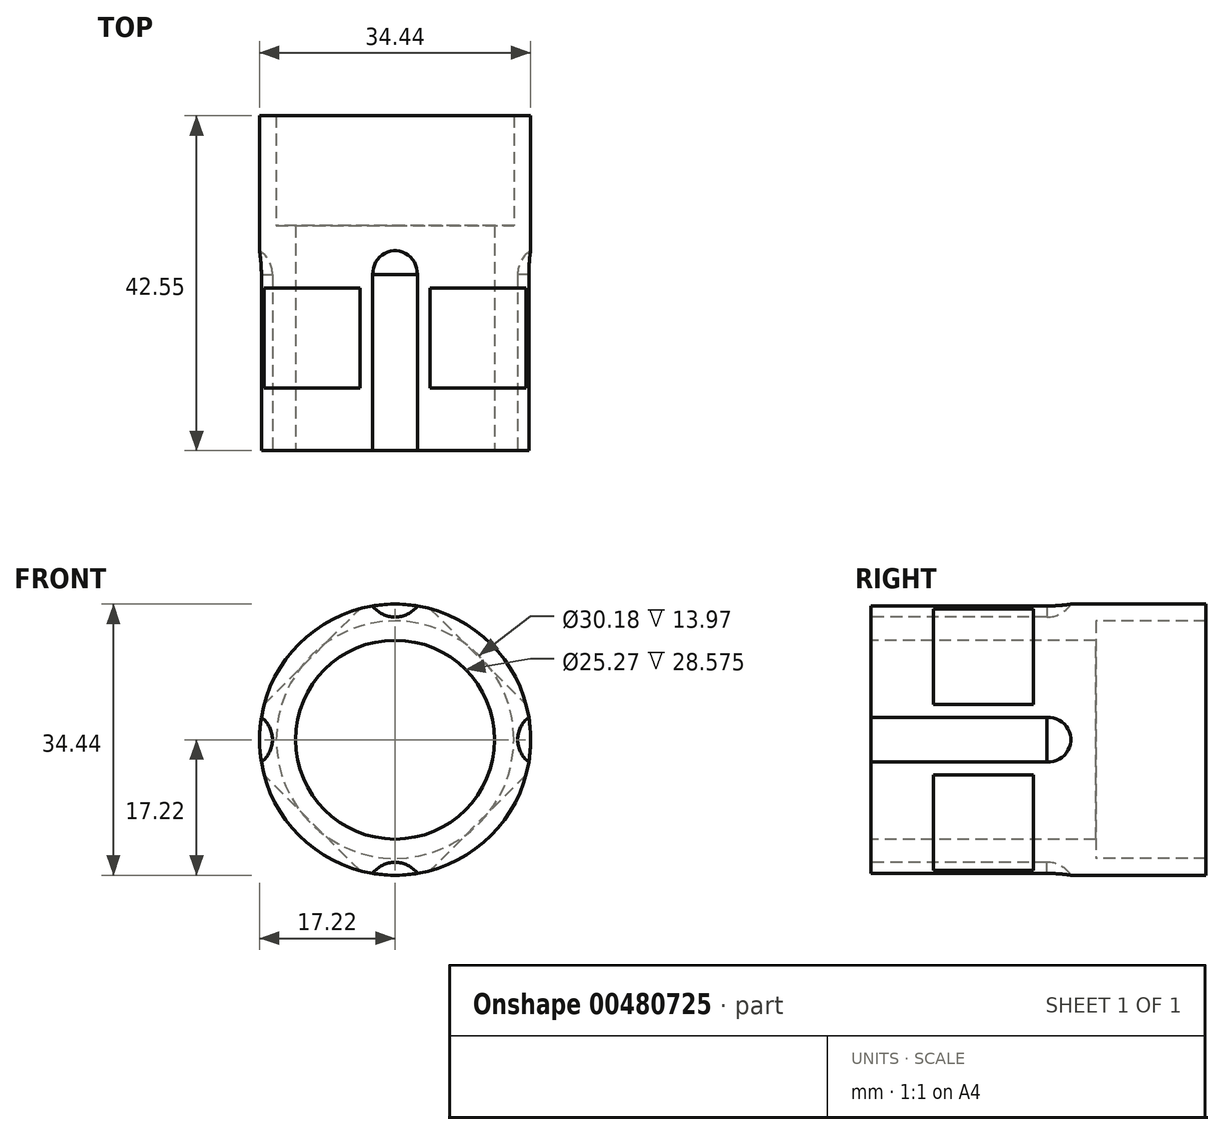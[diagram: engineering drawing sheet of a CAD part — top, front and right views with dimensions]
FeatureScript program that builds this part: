
annotation { "Feature Type Name" : "Feature", "Feature Type Description" : "" }
export const myFeature = defineFeature(function(context is Context, id is Id, definition is map)
    precondition{}
    {
        {
            var Q0;
            Q0=qCreatedBy(makeId("Front.planeOp"),FACE);
            var sketch = newSketch(context, id + "F0", { "sketchPlane" : qUnion([Q0])});
            skCircle(sketch, "E0", {"center": v(0, 0) * mm, "radius": 17.22 * mm});
            skCircle(sketch, "E1.cCircle", {"center": v(0, 0) * mm, "radius": 14.92 * mm, "construction": true});
            skLineSegment(sketch, "E1.0", {"start": v(-4.47, -16.63) * mm, "end": v(-16.63, -4.47) * mm});
            skLineSegment(sketch, "E1.1", {"start": v(-16.63, 4.47) * mm, "end": v(-4.47, 16.63) * mm});
            skLineSegment(sketch, "E1.2", {"start": v(4.47, 16.63) * mm, "end": v(16.63, 4.47) * mm});
            skLineSegment(sketch, "E1.3", {"start": v(16.63, -4.47) * mm, "end": v(4.47, -16.63) * mm});
            skPoint(sketch, "E1.0.midPoint", {"position": v(-10.55, -10.55) * mm});
            skPoint(sketch, "E2.orphan", {"position": v(0, 21.1) * mm});
            skPoint(sketch, "E3.orphan", {"position": v(21.1, 0) * mm});
            skPoint(sketch, "E4.orphan", {"position": v(0, -21.1) * mm});
            skPoint(sketch, "E5.orphan", {"position": v(-21.1, 0) * mm});
            skSolve(sketch);
        }
        {
            var Q0;
            {var subQ0=sQuery(id+"F0.wireOp",EDGE,"E1.0");Q0=makeQuery(id+"F0.imprint","IMPRINT",FACE,{"disambiguationData":[TD([[makeQuery(id+"F0.imprint","IMPRINT",EDGE,{"derivedFrom":subQ0}),-1.0]])]});}
            extrude(context, id + "F1", {"entities" : qUnion([Q0]), "depth" : 12.7 * mm});
        }
        {
            var Q0;
            Q0 = qSketchRegion(id + "F0", true);
            extrude(context, id + "F2", {"entities" : qUnion([Q0]), "operationType" : NewBodyOperationType.ADD, "oppositeDirection" : true, "depth" : 7.94 * mm});
        }
        {
            var Q0;
            Q0=makeQuery(id+"F2.opExtrude","CAP_FACE",FACE,{"disambiguationData":[OSD([sQuery(id+"F0.wireOp",EDGE,"E0")])],"isStart":false});
            var sketch = newSketch(context, id + "F3", { "sketchPlane" : qUnion([Q0])});
            skCircle(sketch, "E6", {"center": v(0, 0) * mm, "radius": 15.09 * mm});
            skSolve(sketch);
        }
        {
            var Q0;
            Q0=makeQuery(id+"F3.imprint","IMPRINT",FACE,{"disambiguationData":[TD([[makeQuery(id+"F3.imprint","IMPRINT",EDGE,{"derivedFrom":sQuery(id+"F3.wireOp",EDGE,"E6")}),-1.0]])]});
            extrude(context, id + "F4", {"entities" : qUnion([Q0]), "operationType" : NewBodyOperationType.ADD, "depth" : 13.97 * mm});
        }
        {
            var Q0;
            Q0=makeQuery(id+"F1.opExtrude","CAP_FACE",FACE,{"disambiguationData":[OSD([sQuery(id+"F0.wireOp",EDGE,"E0"),sQuery(id+"F0.wireOp",EDGE,"E1.0"),sQuery(id+"F0.wireOp",EDGE,"E1.1"),sQuery(id+"F0.wireOp",EDGE,"E1.2"),sQuery(id+"F0.wireOp",EDGE,"E1.3")])],"isStart":false});
            var sketch = newSketch(context, id + "F5", { "sketchPlane" : qUnion([Q0])});
            skCircle(sketch, "E7", {"center": v(0, 0) * mm, "radius": 17.22 * mm});
            skSolve(sketch);
        }
        {
            var Q0;
            Q0 = qSketchRegion(id + "F5", true);
            extrude(context, id + "F6", {"entities" : qUnion([Q0]), "operationType" : NewBodyOperationType.ADD, "depth" : 7.94 * mm});
        }
        {
            var Q0;
            Q0=makeQuery(id+"F6.opExtrude","CAP_FACE",FACE,{"disambiguationData":[OSD([sQuery(id+"F5.wireOp",EDGE,"E7")])],"isStart":false});
            var sketch = newSketch(context, id + "F7", { "sketchPlane" : qUnion([Q0])});
            skCircle(sketch, "E8", {"center": v(0, 0) * mm, "radius": 12.64 * mm});
            skSolve(sketch);
        }
        {
            var Q0;
            Q0 = qSketchRegion(id + "F7", true);
            extrude(context, id + "F8", {"entities" : qUnion([Q0]), "operationType" : NewBodyOperationType.REMOVE, "endBound" : BoundingType.THROUGH_ALL, "oppositeDirection" : true, "depth" : 25.4 * mm});
        }
        {
            var Q0;
            Q0=makeQuery(id+"F6.opExtrude","CAP_FACE",FACE,{"disambiguationData":[OSD([sQuery(id+"F5.wireOp",EDGE,"E7")])],"isStart":false});
            var sketch = newSketch(context, id + "F9", { "sketchPlane" : qUnion([Q0])});
            skCircle(sketch, "E9", {"center": v(-19.14, 0) * mm, "radius": 3.57 * mm});
            skCircle(sketch, "E10", {"center": v(0, 19.14) * mm, "radius": 3.57 * mm});
            skCircle(sketch, "E11", {"center": v(19.14, 0) * mm, "radius": 3.57 * mm});
            skCircle(sketch, "E12", {"center": v(0, -19.14) * mm, "radius": 3.57 * mm});
            skSolve(sketch);
        }
        {
            var Q0;
            Q0 = qSketchRegion(id + "F9", true);
            extrude(context, id + "F10", {"entities" : qUnion([Q0]), "operationType" : NewBodyOperationType.REMOVE, "oppositeDirection" : true, "depth" : 25.4 * mm});
        }
        {
            var Q0;
            Q0=makeQuery(id+"F10.boolean.opBoolean","COPY",EDGE,{"derivedFrom":makeQuery(id+"F10.opExtrude","CAP_EDGE",EDGE,{"disambiguationData":[OSD([sQuery(id+"F9.wireOp",EDGE,"E10")])],"isStart":false})});
            fillet(context, id + "F11", {"entities" : qUnion([Q0]), "radius" : 3.57 * mm, "tangentPropagation" : true, "allowEdgeOverflow" : false});
        }
        {
            var Q0;
            Q0=makeQuery(id+"F10.boolean.opBoolean","COPY",EDGE,{"derivedFrom":makeQuery(id+"F10.opExtrude","CAP_EDGE",EDGE,{"disambiguationData":[OSD([sQuery(id+"F9.wireOp",EDGE,"E9")])],"isStart":false})});
            fillet(context, id + "F12", {"entities" : qUnion([Q0]), "radius" : 3.57 * mm, "tangentPropagation" : true, "allowEdgeOverflow" : false});
        }
        {
            var Q0;
            Q0=makeQuery(id+"F10.boolean.opBoolean","COPY",EDGE,{"derivedFrom":makeQuery(id+"F10.opExtrude","CAP_EDGE",EDGE,{"disambiguationData":[OSD([sQuery(id+"F9.wireOp",EDGE,"E12")])],"isStart":false})});
            fillet(context, id + "F13", {"entities" : qUnion([Q0]), "radius" : 3.57 * mm, "tangentPropagation" : true, "allowEdgeOverflow" : false});
        }
        {
            var Q0;
            Q0=makeQuery(id+"F10.boolean.opBoolean","COPY",EDGE,{"derivedFrom":makeQuery(id+"F10.opExtrude","CAP_EDGE",EDGE,{"disambiguationData":[OSD([sQuery(id+"F9.wireOp",EDGE,"E11")])],"isStart":false})});
            fillet(context, id + "F14", {"entities" : qUnion([Q0]), "radius" : 3.57 * mm, "tangentPropagation" : true, "allowEdgeOverflow" : false});
        }
    });
